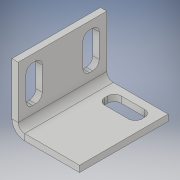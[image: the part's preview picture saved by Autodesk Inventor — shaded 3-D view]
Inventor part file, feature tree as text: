
AUTODESK INVENTOR PART (.ipt)
format: ipt  version: 2017 (Build 210142000, 142)  size: 188,416 bytes
history: native  units: in
note: dims shown in document units (in); Inventor stores cm internally (conversion verified against a paired STEP export)
features: sheet_metal_op x4, sketch x4, extrude x2, other x2
ambient origin geometry x8: Origin, YZ Plane, XZ Plane, XY Plane, X Axis, Y Axis, Z Axis, Center Point
bodies: Solid1 (feature_tree)
feature tree (12):
  sheet_metal_op  "Face1"
  sheet_metal_op  "Flange1"
  sketch  "Sketch3"  dims[d4=0.03in]
  sketch  "Sketch4"  dims[d5=0.12in d6=0.06in d7=0.614in d8=90.0deg d9=0.06in d10=0.24in d11=0.06in d12=0.06in d13=0.539in d14=0.125in d15=0.125in d16=0.154in d17=0.35in d18=0.0625in d19=0.154in d20=0.35in d21=0.0625in d26=0.0625in d28=1.0in d29=0.0in d32=0.154in d33=0.35in d34=0.26in d35=0.15in d36=0.0625in d37=0.154in d38=0.35in d39=0.15in d40=0.26in d41=1.0in d42=0.0in]
  extrude  "Extrusion1"  Depth=0.64in
  extrude  "Extrusion3"  Depth=0.06in
  sketch  "Sketch1"  dims[d0=0.838in d1=0.64in]
  other  "Plate1"
  sketch  "Sketch2"  dims[d2=0.06in d3=0.06in]
  other  "Plate2"
  sheet_metal_op  "Bend1"
  sheet_metal_op  "Corner1"
